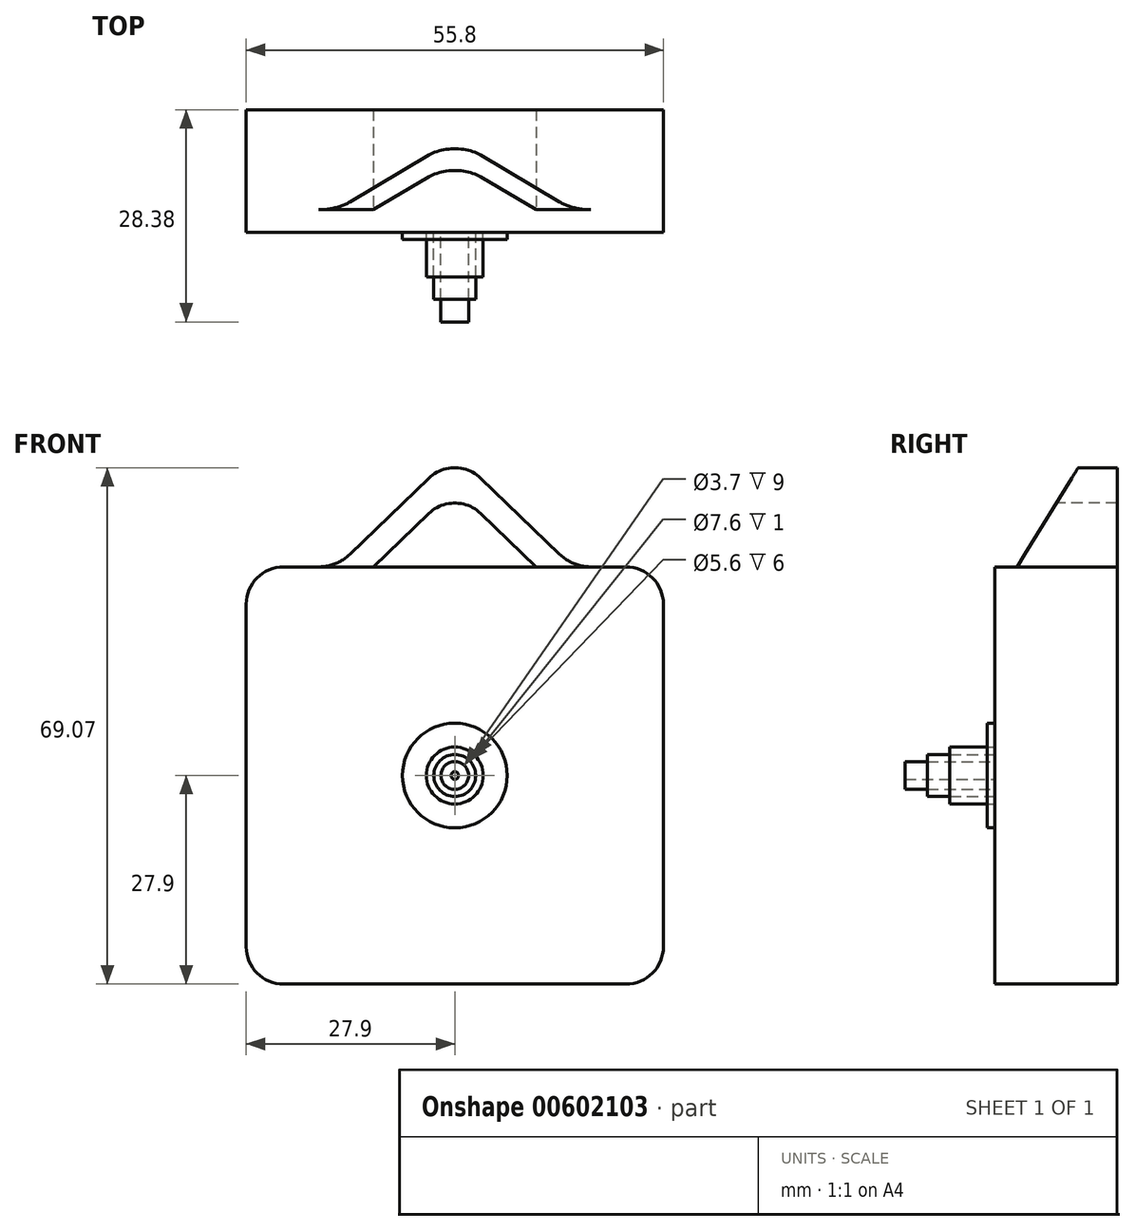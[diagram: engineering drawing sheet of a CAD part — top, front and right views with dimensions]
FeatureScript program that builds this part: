
annotation { "Feature Type Name" : "Feature", "Feature Type Description" : "" }
export const myFeature = defineFeature(function(context is Context, id is Id, definition is map)
    precondition{}
    {
        {
            var Q0;
            Q0=qCreatedBy(makeId("Front.planeOp"),FACE);
            var sketch = newSketch(context, id + "F0", { "sketchPlane" : qUnion([Q0])});
            skLineSegment(sketch, "E0.bottom", {"start": v(22.9, -27.9) * mm, "end": v(-22.9, -27.9) * mm});
            skLineSegment(sketch, "E0.top", {"start": v(-18.19, 27.9) * mm, "end": v(-22.9, 27.9) * mm});
            skLineSegment(sketch, "E0.left", {"start": v(27.9, -22.9) * mm, "end": v(27.9, 22.9) * mm});
            skLineSegment(sketch, "E0.right", {"start": v(-27.9, -22.9) * mm, "end": v(-27.9, 22.9) * mm});
            skPoint(sketch, "E0.middle", {"position": v(0, 0) * mm});
            skLineSegment(sketch, "E1.left", {"start": v(-15.77, 28.41) * mm, "end": v(-15.77, 27.9) * mm});
            skPoint(sketch, "E1.middle", {"position": v(0, 27.9) * mm});
            skLineSegment(sketch, "E2.MirrorCS", {"start": v(27.9, 43.12) * mm, "end": v(-27.9, 43.12) * mm});
            skPoint(sketch, "E3.MirrorP", {"position": v(0, 43.12) * mm});
            skLineSegment(sketch, "E4", {"start": v(-14.02, 29.58) * mm, "end": v(-3.47, 39.77) * mm});
            skLineSegment(sketch, "E5", {"start": v(14.02, 29.58) * mm, "end": v(3.47, 39.77) * mm});
            skPoint(sketch, "E6.newPointA", {"position": v(27.9, 27.9) * mm});
            skPoint(sketch, "E6.newPointB", {"position": v(-15.77, 27.9) * mm});
            skArc(sketch, "E6.filletArc", {"start": v(-18.19, 27.9) * mm, "mid": v(-15.94, 28.34) * mm, "end": v(-14.02, 29.58) * mm});
            skCircle(sketch, "E7", {"center": v(0, 0) * mm, "radius": 7 * mm});
            skCircle(sketch, "E8", {"center": v(0, 0) * mm, "radius": 3.8 * mm});
            skCircle(sketch, "E9", {"center": v(0, 0) * mm, "radius": 2.8 * mm});
            skCircle(sketch, "E10", {"center": v(0, 0) * mm, "radius": 1.85 * mm});
            skLineSegment(sketch, "E11.0", {"start": v(-10.87, 27.9) * mm, "end": v(-3.47, 35.04) * mm});
            skLineSegment(sketch, "E12", {"start": v(0, 7) * mm, "end": v(0, 0) * mm});
            skLineSegment(sketch, "E13.MirrorCS", {"start": v(18.19, 27.9) * mm, "end": v(22.9, 27.9) * mm});
            skPoint(sketch, "E14.MirrorP", {"position": v(15.77, 27.9) * mm});
            skArc(sketch, "E15.MirrorCS", {"start": v(18.19, 27.9) * mm, "mid": v(15.94, 28.34) * mm, "end": v(14.02, 29.58) * mm});
            skLineSegment(sketch, "E16.MirrorCS", {"start": v(10.87, 27.9) * mm, "end": v(3.47, 35.04) * mm});
            skLineSegment(sketch, "E17.trimOffspring", {"start": v(-10.87, 27.9) * mm, "end": v(10.87, 27.9) * mm});
            skPoint(sketch, "E18.orphan", {"position": v(-11.66, 27.14) * mm});
            skPoint(sketch, "E19.orphan", {"position": v(11.66, 27.14) * mm});
            skPoint(sketch, "E20.orphan", {"position": v(15.76, 27.9) * mm});
            skPoint(sketch, "E21.orphan", {"position": v(-2.36, 40.67) * mm});
            skPoint(sketch, "E22.orphan", {"position": v(2.36, 40.67) * mm});
            skArc(sketch, "E23.filletArc", {"start": v(3.47, 39.77) * mm, "mid": v(0, 41.17) * mm, "end": v(-3.47, 39.77) * mm});
            skPoint(sketch, "E24.visualSharp", {"position": v(0, 38.4) * mm});
            skArc(sketch, "E24.filletArc", {"start": v(3.47, 35.04) * mm, "mid": v(0, 36.44) * mm, "end": v(-3.47, 35.04) * mm});
            skPoint(sketch, "E25.orphan", {"position": v(-15.77, 35.5) * mm});
            skPoint(sketch, "E26.orphan", {"position": v(15.76, 35.5) * mm});
            skPoint(sketch, "E1.top.end.orphan", {"position": v(15.76, 20.3) * mm});
            skPoint(sketch, "E1.top.start.orphan", {"position": v(-15.77, 20.3) * mm});
            skArc(sketch, "E27.filletArc", {"start": v(27.9, 22.9) * mm, "mid": v(26.44, 26.44) * mm, "end": v(22.9, 27.9) * mm});
            skPoint(sketch, "E28.visualSharp", {"position": v(-27.9, 27.9) * mm});
            skArc(sketch, "E28.filletArc", {"start": v(-22.9, 27.9) * mm, "mid": v(-26.44, 26.44) * mm, "end": v(-27.9, 22.9) * mm});
            skPoint(sketch, "E29.visualSharp", {"position": v(27.9, -27.9) * mm});
            skArc(sketch, "E29.filletArc", {"start": v(22.9, -27.9) * mm, "mid": v(26.44, -26.44) * mm, "end": v(27.9, -22.9) * mm});
            skPoint(sketch, "E30.visualSharp", {"position": v(-27.9, -27.9) * mm});
            skArc(sketch, "E30.filletArc", {"start": v(-27.9, -22.9) * mm, "mid": v(-26.44, -26.44) * mm, "end": v(-22.9, -27.9) * mm});
            skSolve(sketch);
        }
        {
            var Q0;
            Q0=makeQuery(id+"F0.imprint","IMPRINT",FACE,{"disambiguationData":[TD([[makeQuery(id+"F0.imprint","IMPRINT",EDGE,{"derivedFrom":sQuery(id+"F0.wireOp",EDGE,"E0.bottom")}),-1.0]])]});
            var Q1;
            Q1=makeQuery(id+"F0.imprint","IMPRINT",FACE,{"disambiguationData":[TD([[makeQuery(id+"F0.imprint","IMPRINT",EDGE,{"derivedFrom":sQuery(id+"F0.wireOp",EDGE,"E7")}),1.0]])]});
            var Q2;
            Q2=makeQuery(id+"F0.imprint","IMPRINT",FACE,{"disambiguationData":[TD([[makeQuery(id+"F0.imprint","IMPRINT",EDGE,{"derivedFrom":sQuery(id+"F0.wireOp",EDGE,"E8")}),1.0]])]});
            var Q3;
            Q3=makeQuery(id+"F0.imprint","IMPRINT",FACE,{"disambiguationData":[TD([[makeQuery(id+"F0.imprint","IMPRINT",EDGE,{"derivedFrom":sQuery(id+"F0.wireOp",EDGE,"E9")}),1.0]])]});
            var Q4;
            Q4=makeQuery(id+"F0.imprint","IMPRINT",FACE,{"disambiguationData":[TD([[makeQuery(id+"F0.imprint","IMPRINT",EDGE,{"derivedFrom":sQuery(id+"F0.wireOp",EDGE,"E10")}),1.0]])]});
            extrude(context, id + "F1", {"entities" : qUnion([Q0, Q1, Q2, Q3, Q4]), "oppositeDirection" : true, "depth" : 16.38 * mm, "offsetDistance" : 25 * mm});
        }
        {
            var Q0;
            Q0=qCreatedBy(makeId("Right.planeOp"),FACE);
            cPlane(context, id + "F2", {"entities" : qUnion([Q0]), "cplaneType" : CPlaneType.OFFSET, "offset" : 27.9 * mm, "width" : 150 * mm, "height" : 150 * mm});
        }
        {
            var Q0;
            Q0=qCreatedBy(id+"F2.planeOp",FACE);
            var sketch = newSketch(context, id + "F3", { "sketchPlane" : qUnion([Q0])});
            skPoint(sketch, "E31.0", {"position": v(8.2, 27.9) * mm});
            skPoint(sketch, "E32.0", {"position": v(0, 27.9) * mm});
            skLineSegment(sketch, "E33", {"start": v(0, 27.9) * mm, "end": v(3, 27.9) * mm});
            skLineSegment(sketch, "E34", {"start": v(3, 27.9) * mm, "end": v(13.42, 44.83) * mm});
            skLineSegment(sketch, "E35", {"start": v(13.42, 44.83) * mm, "end": v(0, 44.83) * mm});
            skLineSegment(sketch, "E36", {"start": v(0, 44.83) * mm, "end": v(0, 27.9) * mm});
            skSolve(sketch);
        }
        {
            var Q0;
            Q0=makeQuery(id+"F3.imprint","IMPRINT",FACE,{"disambiguationData":[TD([[makeQuery(id+"F3.imprint","IMPRINT",EDGE,{"derivedFrom":sQuery(id+"F3.wireOp",EDGE,"E33")}),1.0]])]});
            extrude(context, id + "F4", {"entities" : qUnion([Q0]), "operationType" : NewBodyOperationType.REMOVE, "endBound" : BoundingType.THROUGH_ALL, "oppositeDirection" : true, "depth" : 25 * mm, "offsetDistance" : 25 * mm});
        }
        {
            var Q0;
            Q0=makeQuery(id+"F0.imprint","IMPRINT",FACE,{"disambiguationData":[TD([[makeQuery(id+"F0.imprint","IMPRINT",EDGE,{"derivedFrom":sQuery(id+"F0.wireOp",EDGE,"E7")}),1.0]])]});
            extrude(context, id + "F5", {"entities" : qUnion([Q0]), "operationType" : NewBodyOperationType.ADD, "depth" : 1 * mm, "offsetDistance" : 25 * mm});
        }
        {
            var Q0;
            Q0=makeQuery(id+"F0.imprint","IMPRINT",FACE,{"disambiguationData":[TD([[makeQuery(id+"F0.imprint","IMPRINT",EDGE,{"derivedFrom":sQuery(id+"F0.wireOp",EDGE,"E8")}),1.0]])]});
            extrude(context, id + "F6", {"entities" : qUnion([Q0]), "depth" : 6 * mm, "offsetDistance" : 25 * mm});
        }
        {
            var Q0;
            Q0=makeQuery(id+"F0.imprint","IMPRINT",FACE,{"disambiguationData":[TD([[makeQuery(id+"F0.imprint","IMPRINT",EDGE,{"derivedFrom":sQuery(id+"F0.wireOp",EDGE,"E9")}),1.0]])]});
            var sketch = newSketch(context, id + "F7", { "sketchPlane" : qUnion([Q0])});
            skCircle(sketch, "E37", {"center": v(0, 0) * mm, "radius": 0.5 * mm});
            skCircle(sketch, "E38.0", {"center": v(0, 0) * mm, "radius": 1.85 * mm});
            skCircle(sketch, "E39.0", {"center": v(0, 0) * mm, "radius": 2.8 * mm});
            skCircle(sketch, "E40.0", {"center": v(0, 0) * mm, "radius": 1.35 * mm});
            skCircle(sketch, "E41.0", {"center": v(0, 0) * mm, "radius": 1 * mm});
            skSolve(sketch);
        }
        {
            var Q0;
            Q0=makeQuery(id+"F7.imprint","IMPRINT",FACE,{"disambiguationData":[TD([[makeQuery(id+"F7.imprint","IMPRINT",EDGE,{"derivedFrom":sQuery(id+"F7.wireOp",EDGE,"E37")}),1.0]])]});
            var Q1;
            Q1=sQuery(id+"F7.wireOp",EDGE,"E37");
            extrude(context, id + "F8", {"entities" : qUnion([Q0]), "surfaceEntities" : qUnion([Q1]), "depth" : 12 * mm, "offsetDistance" : 25 * mm});
        }
        {
            var Q0;
            Q0=makeQuery(id+"F0.imprint","IMPRINT",FACE,{"disambiguationData":[TD([[makeQuery(id+"F0.imprint","IMPRINT",EDGE,{"derivedFrom":sQuery(id+"F0.wireOp",EDGE,"E9")}),1.0]])]});
            extrude(context, id + "F9", {"entities" : qUnion([Q0]), "depth" : 9 * mm, "offsetDistance" : 25 * mm});
        }
        {
            var Q0;
            Q0=makeQuery(id+"F0.imprint","IMPRINT",FACE,{"disambiguationData":[TD([[makeQuery(id+"F0.imprint","IMPRINT",EDGE,{"derivedFrom":sQuery(id+"F0.wireOp",EDGE,"E10")}),1.0]])]});
            extrude(context, id + "F10", {"entities" : qUnion([Q0]), "depth" : 12 * mm, "offsetDistance" : 25 * mm});
        }
    });
